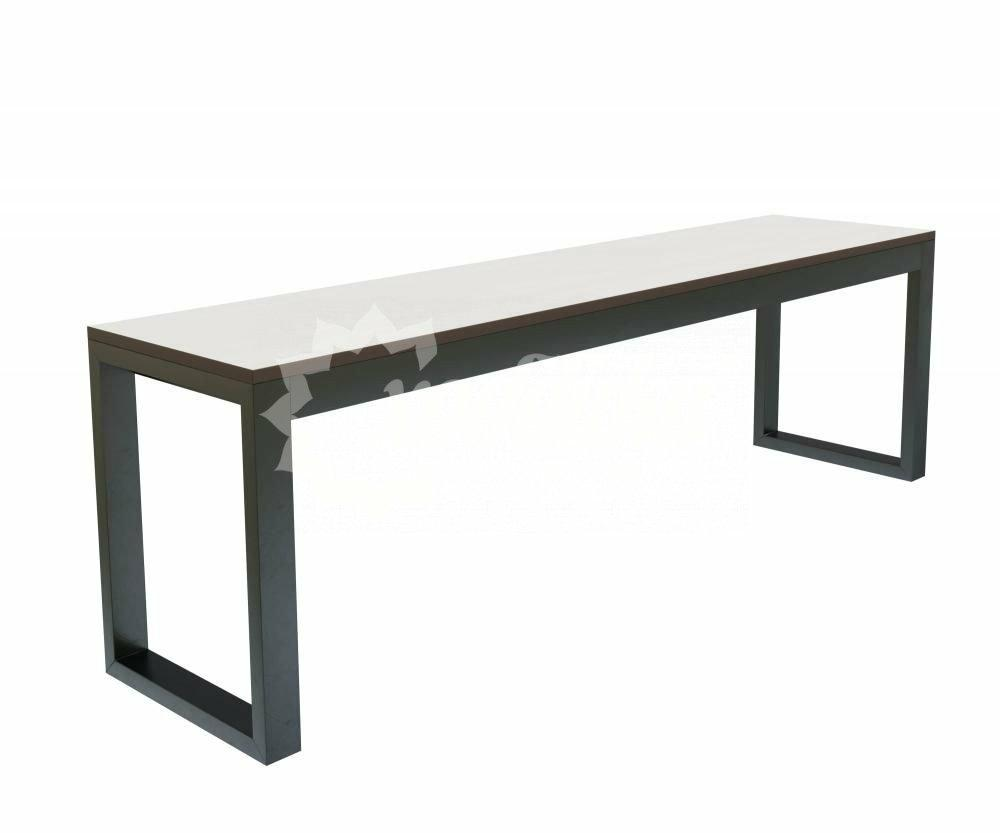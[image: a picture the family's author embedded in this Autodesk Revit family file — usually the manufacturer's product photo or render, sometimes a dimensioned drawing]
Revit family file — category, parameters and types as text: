
# Revit family: Банкетка для раздевалок «Паскаль» Арт 20783
name_source: partatom
category: Антураж
revit_build: Autodesk Revit 2018 (Build: 20180423_1000(x64)
units: mm (PartAtom-declared; Revit-internal decimal feet)

## family parameters
Всегда вертикально = Да
Источник визуального образа = Геометрия семейства
На основе рабочей плоскости = Нет
Общий = Нет
При загрузке вырезать с полостями = Нет
Точка расчета площади = Нет

## types (2) — shared parameters
URL = https://hobbyka.ru
Артикул товара = Арт. 20783
Высота = 450 мм
Группа модели = Скамейки для раздевалок
Изготовитель = ООО «Хоббика»
Изображение типоразмера = Банкетка для раздевалок «Паскаль» Арт 20783.jpg
Материал изделия = Сталь, HPL панели
Цвет каркаса = Сталь
Цвет сидения = HPL панели
Ширина = 400 мм

## per-type parameters (varying)
| type | Версия 1,2 м | Версия 1,5 м | Длина | Описание |
| Версия 1,5 м | Нет | Да | 1500 мм | Банкетка для раздевалок «Паскаль». Версия 1,5 м |
| Версия 1,2 м | Да | Нет | 1200 мм | Банкетка для раздевалок «Паскаль». Версия 1,2 м |
